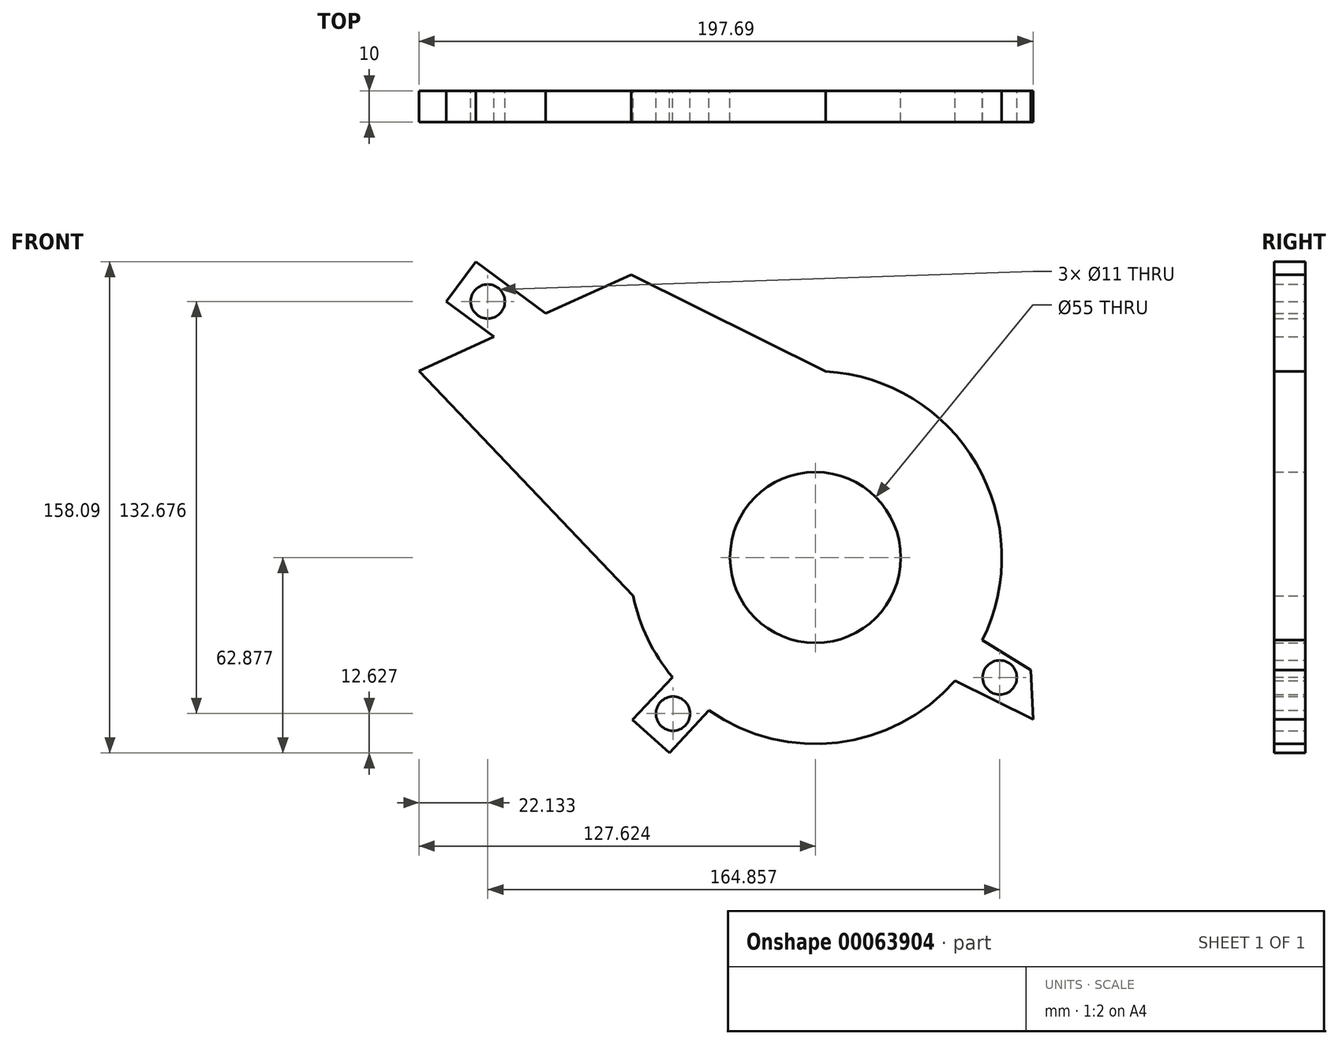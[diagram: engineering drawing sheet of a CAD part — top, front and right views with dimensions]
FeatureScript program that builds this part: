
annotation { "Feature Type Name" : "Feature", "Feature Type Description" : "" }
export const myFeature = defineFeature(function(context is Context, id is Id, definition is map)
    precondition{}
    {
        {
            var Q0;
            Q0=qCreatedBy(makeId("Front.planeOp"),FACE);
            var sketch = newSketch(context, id + "F0", { "sketchPlane" : qUnion([Q0])});
            skCircle(sketch, "E0", {"center": v(30.41, -26.9) * mm, "radius": 60 * mm});
            skLineSegment(sketch, "E1", {"start": v(-28.3, -39.29) * mm, "end": v(-97.2, 33.17) * mm});
            skLineSegment(sketch, "E2", {"start": v(33.77, 33.01) * mm, "end": v(-28.91, 64.17) * mm});
            skLineSegment(sketch, "E3", {"start": v(-28.91, 64.17) * mm, "end": v(-97.2, 33.17) * mm});
            skCircle(sketch, "E4", {"center": v(30.41, -26.9) * mm, "radius": 27.5 * mm});
            skLineSegment(sketch, "E5", {"start": v(-73.04, 44.14) * mm, "end": v(-88.44, 55.53) * mm});
            skLineSegment(sketch, "E6", {"start": v(-88.44, 55.53) * mm, "end": v(-78.98, 68.32) * mm});
            skLineSegment(sketch, "E7", {"start": v(-78.98, 68.32) * mm, "end": v(-56.48, 51.66) * mm});
            skCircle(sketch, "E8", {"center": v(-75.08, 55.53) * mm, "radius": 5.5 * mm});
            skLineSegment(sketch, "E9", {"start": v(100.48, -79.03) * mm, "end": v(75.4, -66.6) * mm});
            skLineSegment(sketch, "E10", {"start": v(100.48, -79.03) * mm, "end": v(99.75, -63.15) * mm});
            skLineSegment(sketch, "E11", {"start": v(99.75, -63.15) * mm, "end": v(84.2, -53.47) * mm});
            skCircle(sketch, "E12", {"center": v(89.78, -65.49) * mm, "radius": 5.5 * mm});
            skLineSegment(sketch, "E13", {"start": v(-15.6, -65.4) * mm, "end": v(-28.47, -79.15) * mm});
            skLineSegment(sketch, "E14", {"start": v(-16.62, -89.77) * mm, "end": v(-3.88, -76.13) * mm});
            skLineSegment(sketch, "E15", {"start": v(-28.47, -79.15) * mm, "end": v(-16.62, -89.77) * mm});
            skCircle(sketch, "E16", {"center": v(-15.43, -77.14) * mm, "radius": 5.5 * mm});
            skSolve(sketch);
        }
        {
            var Q0;
            {var subQ3=sQuery(id+"F0.wireOp",EDGE,"E1");Q0=makeQuery(id+"F0.imprint","IMPRINT",FACE,{"disambiguationData":[TD([[makeQuery(id+"F0.imprint","IMPRINT",EDGE,{"derivedFrom":subQ3}),-1.0]])]});}
            var Q1;
            Q1=makeQuery(id+"F0.imprint","IMPRINT",FACE,{"disambiguationData":[TD([[makeQuery(id+"F0.imprint","IMPRINT",EDGE,{"derivedFrom":sQuery(id+"F0.wireOp",EDGE,"E4")}),-1.0]])]});
            var Q2;
            {var subQ0=sQuery(id+"F0.wireOp",EDGE,"E9");Q2=makeQuery(id+"F0.imprint","IMPRINT",FACE,{"disambiguationData":[TD([[makeQuery(id+"F0.imprint","IMPRINT",EDGE,{"derivedFrom":subQ0}),-1.0]])]});}
            var Q3;
            {var subQ1=sQuery(id+"F0.wireOp",EDGE,"E5");Q3=makeQuery(id+"F0.imprint","IMPRINT",FACE,{"disambiguationData":[TD([[makeQuery(id+"F0.imprint","IMPRINT",EDGE,{"derivedFrom":subQ1}),-1.0]])]});}
            extrude(context, id + "F1", {"entities" : qUnion([Q0, Q1, Q2, Q3]), "depth" : 10 * mm});
        }
        {
            var Q0;
            {var subQ0=sQuery(id+"F0.wireOp",EDGE,"E13");Q0=makeQuery(id+"F0.imprint","IMPRINT",FACE,{"disambiguationData":[TD([[makeQuery(id+"F0.imprint","IMPRINT",EDGE,{"derivedFrom":subQ0}),1.0]])]});}
            extrude(context, id + "F2", {"entities" : qUnion([Q0]), "operationType" : NewBodyOperationType.ADD, "depth" : 10 * mm});
        }
    });
